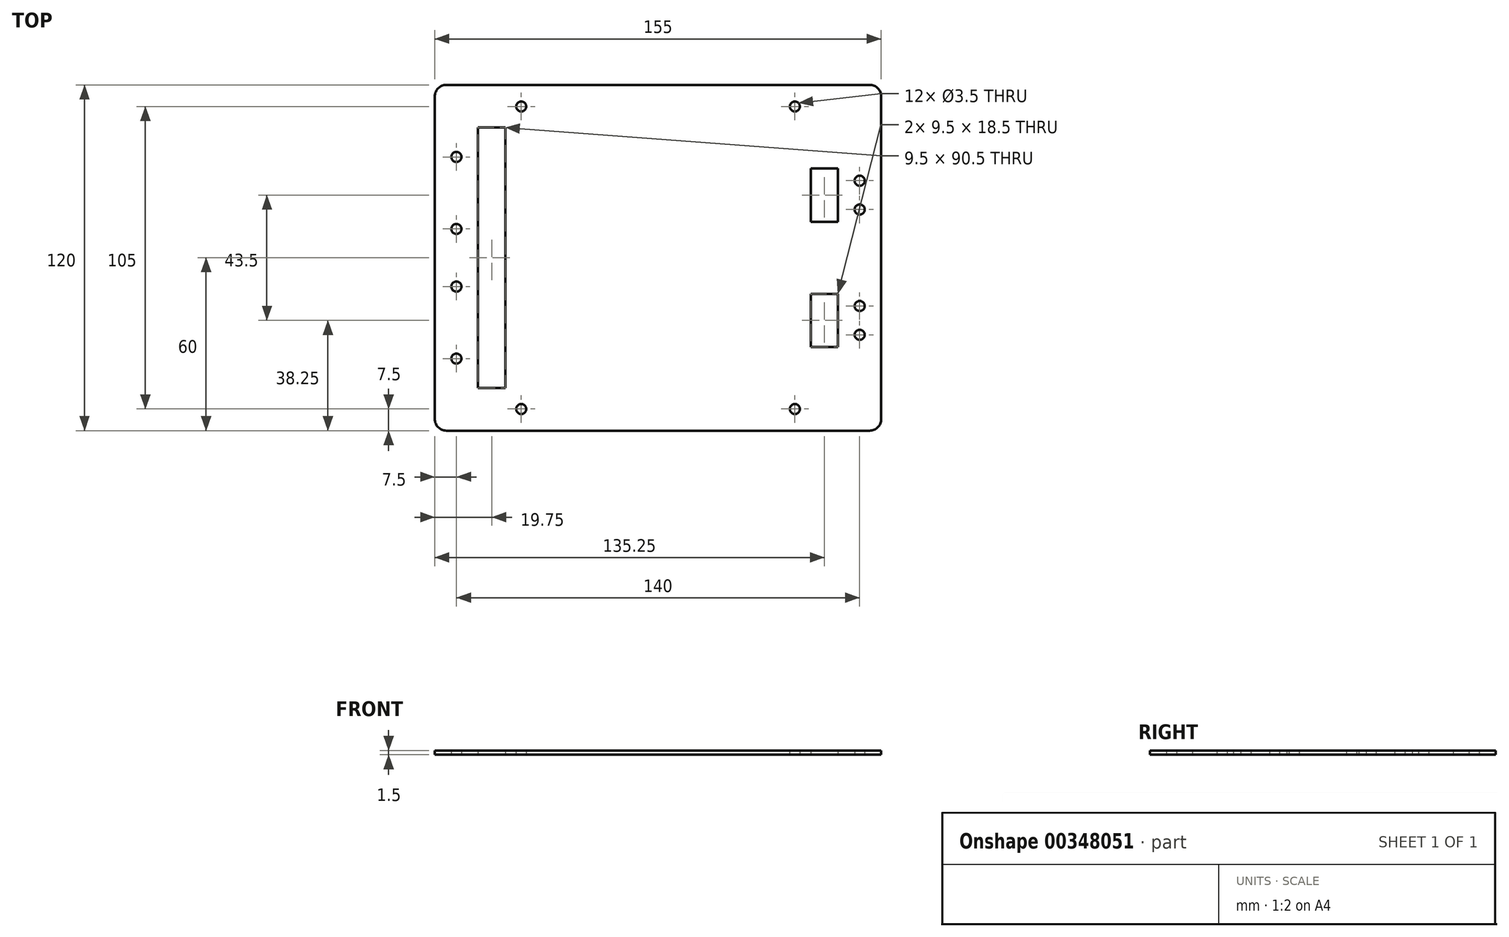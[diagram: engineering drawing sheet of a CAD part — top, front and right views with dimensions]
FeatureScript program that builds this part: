
annotation { "Feature Type Name" : "Feature", "Feature Type Description" : "" }
export const myFeature = defineFeature(function(context is Context, id is Id, definition is map)
    precondition{}
    {
        {
            var Q0;
            Q0=qCreatedBy(makeId("Top.planeOp"),FACE);
            var sketch = newSketch(context, id + "F0", { "sketchPlane" : qUnion([Q0])});
            skLineSegment(sketch, "E0.bottom", {"start": v(-73.5, 60) * mm, "end": v(73.5, 60) * mm});
            skLineSegment(sketch, "E0.top", {"start": v(-73.5, -60) * mm, "end": v(73.5, -60) * mm});
            skLineSegment(sketch, "E0.left", {"start": v(-77.5, 56) * mm, "end": v(-77.5, -56) * mm});
            skLineSegment(sketch, "E0.right", {"start": v(77.5, 56) * mm, "end": v(77.5, -56) * mm});
            skPoint(sketch, "E0.middle", {"position": v(0, 0) * mm});
            skPoint(sketch, "E1.visualSharp", {"position": v(-77.5, 60) * mm});
            skArc(sketch, "E1.filletArc", {"start": v(-73.5, 60) * mm, "mid": v(-76.33, 58.83) * mm, "end": v(-77.5, 56) * mm});
            skPoint(sketch, "E2.visualSharp", {"position": v(-77.5, -60) * mm});
            skArc(sketch, "E2.filletArc", {"start": v(-77.5, -56) * mm, "mid": v(-76.33, -58.83) * mm, "end": v(-73.5, -60) * mm});
            skPoint(sketch, "E3.visualSharp", {"position": v(77.5, 60) * mm});
            skArc(sketch, "E3.filletArc", {"start": v(77.5, 56) * mm, "mid": v(76.33, 58.83) * mm, "end": v(73.5, 60) * mm});
            skPoint(sketch, "E4.visualSharp", {"position": v(77.5, -60) * mm});
            skArc(sketch, "E4.filletArc", {"start": v(73.5, -60) * mm, "mid": v(76.33, -58.83) * mm, "end": v(77.5, -56) * mm});
            skCircle(sketch, "E5", {"center": v(-47.5, 52.5) * mm, "radius": 1.75 * mm});
            skLineSegment(sketch, "E6", {"start": v(-47.5, 52.5) * mm, "end": v(-77.5, 52.5) * mm, "construction": true});
            skCircle(sketch, "E7.MirrorC", {"center": v(47.5, 52.5) * mm, "radius": 1.75 * mm});
            skCircle(sketch, "E8.MirrorC", {"center": v(47.5, -52.5) * mm, "radius": 1.75 * mm});
            skCircle(sketch, "E9.MirrorC", {"center": v(-47.5, -52.5) * mm, "radius": 1.75 * mm});
            skCircle(sketch, "E10", {"center": v(-70, -35) * mm, "radius": 1.75 * mm});
            skCircle(sketch, "E11.MirrorC", {"center": v(-70, 35) * mm, "radius": 1.75 * mm});
            skCircle(sketch, "E12", {"center": v(-70, -10) * mm, "radius": 1.75 * mm});
            skCircle(sketch, "E13.MirrorC", {"center": v(-70, 10) * mm, "radius": 1.75 * mm});
            skLineSegment(sketch, "E14.top", {"start": v(-62.5, -45.25) * mm, "end": v(-53, -45.25) * mm});
            skLineSegment(sketch, "E15.MirrorCS", {"start": v(-62.5, 45.25) * mm, "end": v(-53, 45.25) * mm});
            skLineSegment(sketch, "E16", {"start": v(-62.5, -45.25) * mm, "end": v(-62.5, 45.25) * mm});
            skLineSegment(sketch, "E17", {"start": v(-53, 45.25) * mm, "end": v(-53, -45.25) * mm});
            skLineSegment(sketch, "E18.bottom", {"start": v(53, -12.5) * mm, "end": v(62.5, -12.5) * mm});
            skLineSegment(sketch, "E18.top", {"start": v(53, -31) * mm, "end": v(62.5, -31) * mm});
            skLineSegment(sketch, "E18.left", {"start": v(53, -12.5) * mm, "end": v(53, -31) * mm});
            skLineSegment(sketch, "E18.right", {"start": v(62.5, -12.5) * mm, "end": v(62.5, -31) * mm});
            skLineSegment(sketch, "E19.MirrorCS", {"start": v(53, 12.5) * mm, "end": v(62.5, 12.5) * mm});
            skLineSegment(sketch, "E20.MirrorCS", {"start": v(53, 12.5) * mm, "end": v(53, 31) * mm});
            skLineSegment(sketch, "E21.MirrorCS", {"start": v(62.5, 12.5) * mm, "end": v(62.5, 31) * mm});
            skLineSegment(sketch, "E22.MirrorCS", {"start": v(53, 31) * mm, "end": v(62.5, 31) * mm});
            skCircle(sketch, "E23", {"center": v(70, 26.75) * mm, "radius": 1.75 * mm});
            skCircle(sketch, "E24", {"center": v(70, 16.75) * mm, "radius": 1.75 * mm});
            skCircle(sketch, "E25.MirrorC", {"center": v(70, -16.75) * mm, "radius": 1.75 * mm});
            skCircle(sketch, "E26.MirrorC", {"center": v(70, -26.75) * mm, "radius": 1.75 * mm});
            skSolve(sketch);
        }
        {
            var Q0;
            Q0=makeQuery(id+"F0.imprint","IMPRINT",FACE,{"disambiguationData":[TD([[makeQuery(id+"F0.imprint","IMPRINT",EDGE,{"derivedFrom":sQuery(id+"F0.wireOp",EDGE,"E0.bottom")}),-1.0]])]});
            extrude(context, id + "F1", {"entities" : qUnion([Q0]), "depth" : 1.5 * mm});
        }
    });
